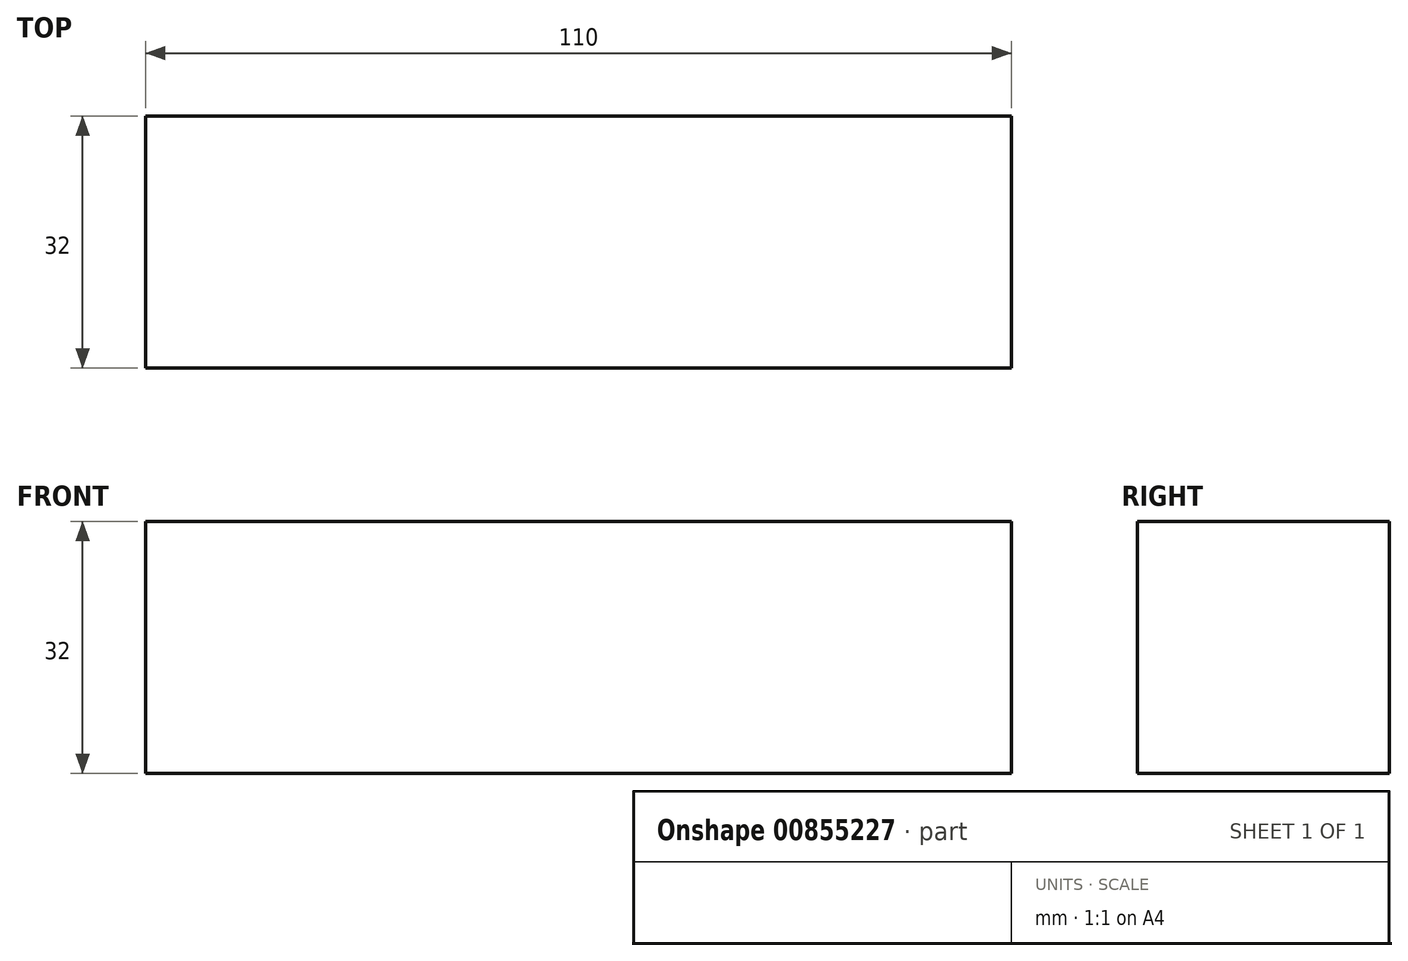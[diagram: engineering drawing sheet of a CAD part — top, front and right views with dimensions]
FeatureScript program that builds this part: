
annotation { "Feature Type Name" : "Feature", "Feature Type Description" : "" }
export const myFeature = defineFeature(function(context is Context, id is Id, definition is map)
    precondition{}
    {
        {
            var Q0;
            Q0=qCreatedBy(makeId("Right.planeOp"),FACE);
            var sketch = newSketch(context, id + "F0", { "sketchPlane" : qUnion([Q0])});
            skLineSegment(sketch, "E0.bottom", {"start": v(0, 0) * mm, "end": v(32, 0) * mm});
            skLineSegment(sketch, "E0.top", {"start": v(0, 32) * mm, "end": v(32, 32) * mm});
            skLineSegment(sketch, "E0.left", {"start": v(0, 0) * mm, "end": v(0, 32) * mm});
            skLineSegment(sketch, "E0.right", {"start": v(32, 0) * mm, "end": v(32, 32) * mm});
            skSolve(sketch);
        }
        {
            var Q0;
            Q0=makeQuery(id+"F0.imprint","IMPRINT",FACE,{"disambiguationData":[TD([[makeQuery(id+"F0.imprint","IMPRINT",EDGE,{"derivedFrom":sQuery(id+"F0.wireOp",EDGE,"E0.bottom")}),1.0]])]});
            extrude(context, id + "F1", {"entities" : qUnion([Q0]), "depth" : 110 * mm, "offsetDistance" : 25 * mm});
        }
    });
